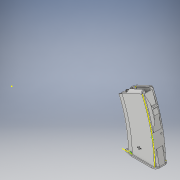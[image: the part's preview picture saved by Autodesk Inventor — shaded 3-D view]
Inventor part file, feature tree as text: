
AUTODESK INVENTOR PART (.ipt)
format: ipt  version: 2017 (Build 210142000, 142)  size: 622,592 bytes
history: native  units: in
note: dims shown in document units (in); Inventor stores cm internally (conversion verified against a paired STEP export)
features: sketch x24, extrude x19, plane x5, fillet x3, chamfer x2, sweep x1, shell x1
ambient origin geometry x8: Origin, YZ Plane, XZ Plane, XY Plane, X Axis, Y Axis, Z Axis, Center Point
bodies: Solid1 (feature_tree)
feature tree (55):
  sweep  "Sweep1"
  shell  "Shell1"  Thickness=0.0787in
  extrude  "Extrusion1"  TaperAngle=0.0deg  [1 undecoded]
  sketch  "Sketch4"  dims[d29=90.0deg d31=0.4134in]
  extrude  "Extrusion2"  TaperAngle=90.0deg  [1 undecoded]
  plane  "Work Plane1"
  extrude  "Extrusion3"  Depth=0.4134in
  plane  "Work Plane2"
  plane  "Work Plane3"
  extrude  "Extrusion4"  Depth=0.1083in TaperAngle=0.0deg
  sketch  "Sketch12"  dims[d40=0.3556in d41=0.3682in]
  extrude  "Extrusion6"  Depth=0.1575in
  extrude  "Extrusion7"  Depth=0.3682in
  extrude  "Extrusion8"  Depth=0.2559in
  extrude  "Extrusion9"  Depth=0.2559in
  extrude  "Extrusion10"  Depth=0.3937in
  extrude  "Extrusion11"  Depth=0.3937in TaperAngle=0.0deg
  sketch  "Sketch26"  dims[d55=0.1969in d56=0.0591in]
  plane  "Work Plane4"
  extrude  "Extrusion12"  Depth=0.0591in
  chamfer  "Chamfer1"  Distance=3.937in
  sketch  "Sketch28"  dims[d59=135.0deg d62=3.937in d63=0.0in]
  extrude  "Extrusion13"  Depth=0.2175in
  fillet  "Fillet1"  Radius=0.2776in
  extrude  "Extrusion14"  Depth=1.8504in TaperAngle=0.0deg
  extrude  "Extrusion15"  Depth=0.3937in
  sketch  "Sketch34"  dims[d70=1.8504in d71=0.0in d73=0.3937in]
  sketch  "Sketch35"  dims[d74=1.8504in d75=0.0in d79=0.1969in]
  extrude  "Extrusion16"  Depth=0.1969in
  extrude  "Extrusion17"  Depth=0.3937in TaperAngle=0.0deg
  extrude  "Extrusion18"  Depth=0.4921in
  extrude  "Extrusion19"  Depth=0.0984in
  sketch  "Sketch39"  dims[d93=0.4724in]
  chamfer  "Chamfer2"  Distance=0.3937in
  sketch  "Sketch40"  dims[d94=0.1575in]
  plane  "Work Plane6"
  extrude  "Extrusion20"  Depth=0.0394in TaperAngle=45.0deg
  fillet  "Fillet2"  Radius=1.1811in
  fillet  "Fillet3"  Radius=0.7087in
  sketch  "Sketch1"  dims[d0=1.6929in d1=0.7874in d4=0.0787in]
  sketch  "Sketch2"  dims[d6=0.0787in d20=0.0in d21=0.0in]
  sketch  "Sketch3"  dims[d22=0.0787in d27=90.0deg]
  sketch  "Sketch7"  dims[d32=0.4134in d33=0.1083in d34=0.0in]
  sketch  "Sketch11"  dims[d35=1.2598in d38=0.1575in]
  sketch  "Sketch15"  dims[d42=3.937in d43=0.0in d46=0.2559in]
  sketch  "Sketch18"  dims[d47=90.0deg d48=0.2559in]
  sketch  "Sketch21"  dims[d49=0.3937in d50=0.0in d51=0.2165in]
  sketch  "Sketch25"  dims[d52=0.2165in d53=0.3937in d54=0.0in]
  sketch  "Sketch27"  dims[d58=0.1969in]
  sketch  "Sketch31"  dims[d64=0.2175in d65=0.2175in d66=0.2776in]
  sketch  "Sketch33"  dims[d67=0.2776in d68=1.8504in d69=0.0in]
  sketch  "Sketch36"  dims[d80=0.3937in d83=0.2756in d84=0.0in]
  sketch  "Sketch37"  dims[d85=2.3622in d86=0.0in d87=0.4921in]
  sketch  "Sketch38"  dims[d88=2.874in d91=0.0984in]
  sketch  "Sketch41"  dims[d95=0.1772in d96=0.3937in d97=0.0in d98=0.1417in d99=0.0787in d100=45.0deg d101=1.1811in d102=0.7087in d103=0.0in d104=0.1181in d106=0.2362in d107=0.0in d108=0.0197in d109=0.0in d111=0.315in d112=0.0984in d113=0.1772in d114=0.3937in d115=0.0in d116=0.3937in d117=0.0in d118=0.2362in d119=0.0in d120=0.2362in d121=0.0in d124=0.0787in d125=0.0394in d126=45.0deg d127=0.1181in d128=0.1181in d129=0.0in d133=0.0394in d134=0.0394in]
note: 2 required parameter values undecoded (feature->parameter linkage not recoverable at this tier; creation-order binding heuristic only, values carry confidence <= 0.55)
